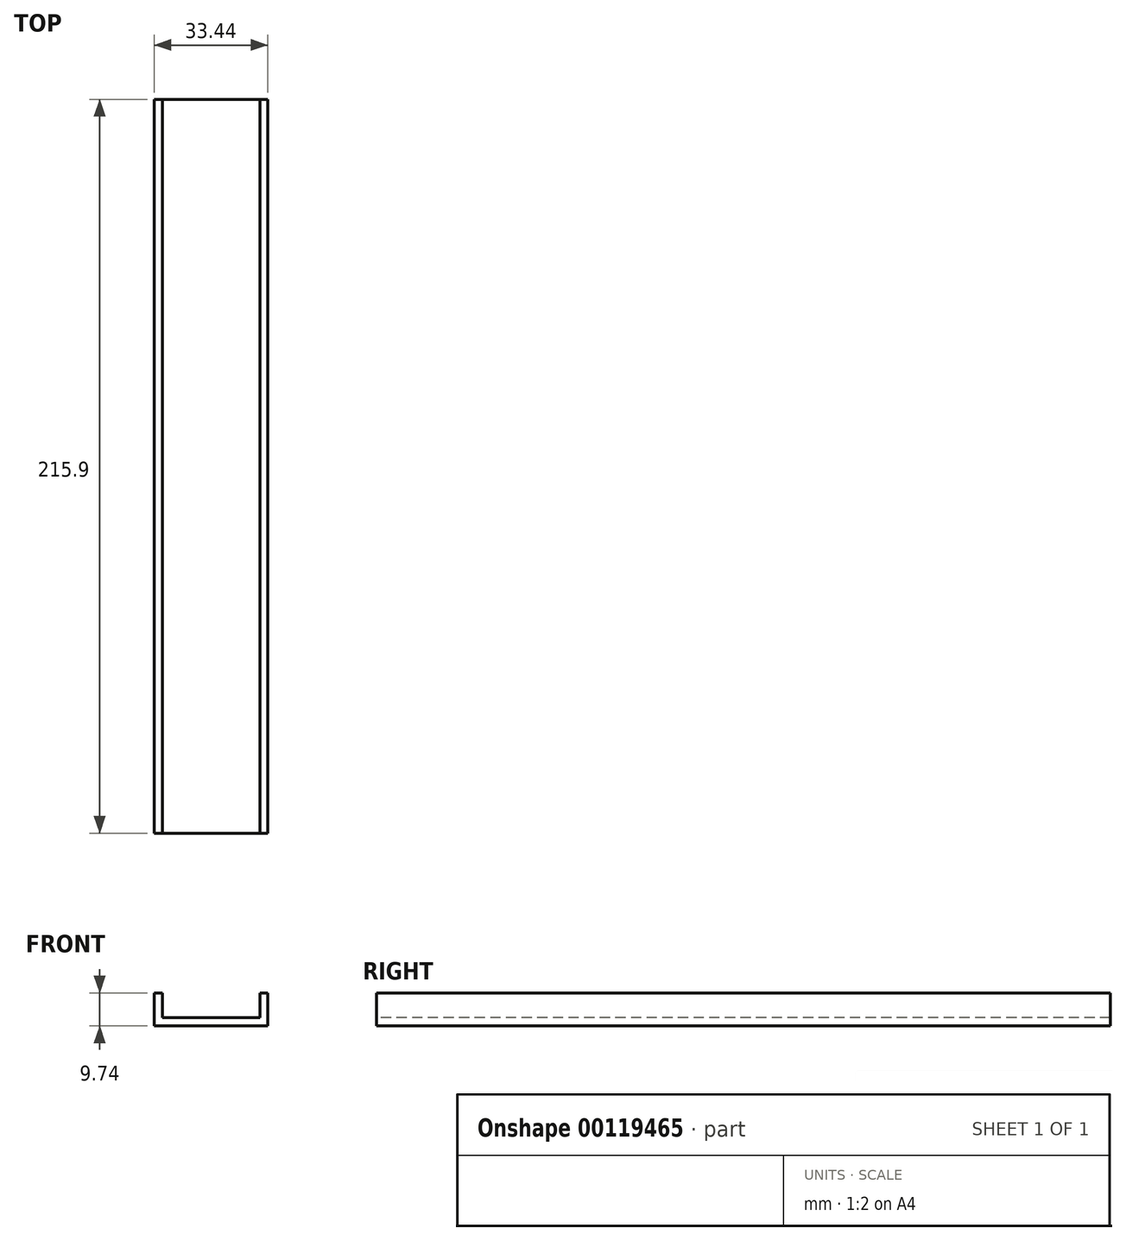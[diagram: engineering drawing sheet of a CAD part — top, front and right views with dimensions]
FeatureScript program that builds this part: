
annotation { "Feature Type Name" : "Feature", "Feature Type Description" : "" }
export const myFeature = defineFeature(function(context is Context, id is Id, definition is map)
    precondition{}
    {
        {
            var Q0;
            Q0=qCreatedBy(makeId("Front.planeOp"),FACE);
            var sketch = newSketch(context, id + "F0", { "sketchPlane" : qUnion([Q0])});
            skLineSegment(sketch, "E0.bottom", {"start": v(-16.72, -4.87) * mm, "end": v(16.72, -4.87) * mm});
            skLineSegment(sketch, "E0.top", {"start": v(-16.72, 4.87) * mm, "end": v(16.72, 4.87) * mm});
            skLineSegment(sketch, "E0.left", {"start": v(-16.72, -4.87) * mm, "end": v(-16.72, 4.87) * mm});
            skLineSegment(sketch, "E0.right", {"start": v(16.72, -4.87) * mm, "end": v(16.72, 4.87) * mm});
            skPoint(sketch, "E0.middle", {"position": v(0, 0) * mm});
            skSolve(sketch);
        }
        {
            var Q0;
            Q0=makeQuery(id+"F0.imprint","IMPRINT",FACE,{"disambiguationData":[TD([[makeQuery(id+"F0.imprint","IMPRINT",EDGE,{"derivedFrom":sQuery(id+"F0.wireOp",EDGE,"E0.bottom")}),1.0]])]});
            extrude(context, id + "F1", {"entities" : qUnion([Q0]), "depth" : 215.9 * mm});
        }
        {
            var Q0;
            Q0=makeQuery(id+"F1.opExtrude","CAP_FACE",FACE,{"disambiguationData":[OSD([sQuery(id+"F0.wireOp",EDGE,"E0.bottom"),sQuery(id+"F0.wireOp",EDGE,"E0.top"),sQuery(id+"F0.wireOp",EDGE,"E0.left"),sQuery(id+"F0.wireOp",EDGE,"E0.right")])],"isStart":false});
            var sketch = newSketch(context, id + "F2", { "sketchPlane" : qUnion([Q0])});
            skLineSegment(sketch, "E1.bottom", {"start": v(-14.26, 4.87) * mm, "end": v(14.44, 4.87) * mm});
            skLineSegment(sketch, "E1.top", {"start": v(-14.26, -2.37) * mm, "end": v(14.44, -2.37) * mm});
            skLineSegment(sketch, "E1.left", {"start": v(-14.26, 4.87) * mm, "end": v(-14.26, -2.37) * mm});
            skLineSegment(sketch, "E1.right", {"start": v(14.44, 4.87) * mm, "end": v(14.44, -2.37) * mm});
            skSolve(sketch);
        }
        {
            var Q0;
            Q0=makeQuery(id+"F2.imprint","IMPRINT",FACE,{"disambiguationData":[TD([[makeQuery(id+"F2.imprint","IMPRINT",EDGE,{"derivedFrom":sQuery(id+"F2.wireOp",EDGE,"E1.bottom")}),-1.0]])]});
            extrude(context, id + "F3", {"entities" : qUnion([Q0]), "operationType" : NewBodyOperationType.REMOVE, "oppositeDirection" : true, "depth" : 218.44 * mm});
        }
    });
